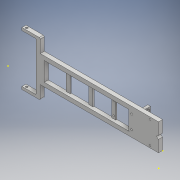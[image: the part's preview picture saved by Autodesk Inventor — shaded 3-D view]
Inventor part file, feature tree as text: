
AUTODESK INVENTOR PART (.ipt)
format: ipt  version: 2018 (Build 220112000, 112)  size: 670,208 bytes
history: native  units: mm
features: sketch x36, extrude x27, fillet x10, hole x6
ambient origin geometry x8: Origin, YZ Plane, XZ Plane, XY Plane, X Axis, Y Axis, Z Axis, Center Point
bodies: Solid1 (feature_tree)
feature tree (79):
  extrude  "Extrusion1"  Depth=50.0mm
  hole  "Hole1"  [1 undecoded]
  hole  "Hole2"  [1 undecoded]
  extrude  "Extrusion2"  Depth=25.0mm
  extrude  "Extrusion3"  Depth=25.0mm
  extrude  "Extrusion4"  Depth=5.0mm
  sketch  "Sketch7"  dims[d25=10.0mm d26=5.0mm]
  extrude  "Extrusion5"  Depth=5.0mm
  extrude  "Extrusion6"  Depth=35.0mm
  extrude  "Extrusion7"  Depth=35.0mm
  extrude  "Extrusion8"  Depth=35.0mm
  extrude  "Extrusion9"  Depth=2.0mm TaperAngle=0.0deg
  extrude  "Extrusion10"  Depth=7.5mm TaperAngle=0.0deg
  extrude  "Extrusion11"  Depth=10.0mm
  extrude  "Extrusion12"  Depth=7.5mm
  fillet  "Fillet1"  Radius=7.5mm
  fillet  "Fillet2"  Radius=25.0mm
  fillet  "Fillet3"  Radius=3.0mm
  fillet  "Fillet4"  Radius=3.2mm
  fillet  "Fillet5"  Radius=2.1mm
  fillet  "Fillet6"  Radius=5.5mm
  extrude  "Extrusion13"  Depth=92.5mm TaperAngle=0.0deg
  sketch  "Sketch17"  dims[d58=4.25mm d59=241.0mm d60=0.0mm]
  hole  "Hole3"  [1 undecoded]
  hole  "Hole4"  [1 undecoded]
  extrude  "Extrusion14"  Depth=5.0mm
  extrude  "Extrusion15"  Depth=91.25mm TaperAngle=0.0deg
  extrude  "Extrusion16"  Depth=30.0mm
  extrude  "Extrusion17"  Depth=2.5mm
  extrude  "Extrusion18"  Depth=14.55mm TaperAngle=0.0deg
  extrude  "Extrusion19"  Depth=0.1mm
  extrude  "Extrusion20"  Depth=3.25mm
  extrude  "Extrusion21"  Depth=3.25mm
  hole  "Hole5"  [1 undecoded]
  extrude  "Extrusion22"  Depth=2.0mm
  extrude  "Extrusion23"  Depth=15.0mm
  extrude  "Extrusion24"  Depth=10.0mm TaperAngle=0.0deg
  extrude  "Extrusion25"  Depth=2.0mm
  extrude  "Extrusion26"  Depth=100.0mm TaperAngle=0.0deg
  sketch  "Sketch34"  dims[d113=5.0mm d114=2.0mm d115=0.0mm]
  hole  "Hole6"  [1 undecoded]
  extrude  "Extrusion27"  Depth=5.5mm
  fillet  "Fillet7"  Radius=3.3mm
  fillet  "Fillet8"  Radius=3.3mm
  fillet  "Fillet9"  Radius=2.0mm
  fillet  "Fillet10"  Radius=5.5mm
  sketch  "Sketch1"  dims[d0=50.0mm d1=50.0mm]
  sketch  "Sketch2"  dims[d2=240.0mm d3=7.5mm]
  sketch  "Sketch3"  dims[d4=7.5mm d5=7.5mm d6=0.0mm]
  sketch  "Sketch4"  dims[d7=6.35mm d8=6.0mm d9=4.0mm d10=2.0mm d11=90.0deg d12=8.0mm d13=20.594885mm d14=25.0mm]
  sketch  "Sketch5"  dims[d15=3.3mm d16=6.0mm d17=4.0mm d18=2.0mm d19=90.0deg d20=8.0mm d21=20.594885mm d22=25.0mm]
  sketch  "Sketch6"  dims[d23=180.0deg d24=5.0mm]
  sketch  "Sketch8"  dims[d27=17.5mm d28=0.0mm d30=35.0mm]
  sketch  "Sketch9"  dims[d31=35.0mm d32=35.0mm]
  sketch  "Sketch10"  dims[d33=35.0mm d34=35.0mm]
  sketch  "Sketch11"  dims[d35=35.0mm d36=2.0mm d37=0.0mm]
  sketch  "Sketch12"  dims[d38=10.0mm d39=7.5mm d40=0.0mm]
  sketch  "Sketch13"  dims[d41=100.0mm d42=10.0mm]
  sketch  "Sketch14"  dims[d43=7.5mm d44=0.0mm d45=7.5mm d46=7.5mm d47=25.0mm d48=0.0mm d49=3.0mm d50=3.2mm d51=2.1mm d52=5.5mm]
  sketch  "Sketch15"  dims[d53=3.3mm d54=92.5mm d55=0.0mm]
  sketch  "Sketch16"  dims[d56=5.5mm d57=3.3mm]
  sketch  "Sketch18"  dims[d61=4.44mm d62=5.0mm]
  sketch  "Sketch19"  dims[d63=2.5mm d64=91.25mm d65=0.0mm]
  sketch  "Sketch20"  dims[d66=30.0mm d67=6.35mm]
  sketch  "Sketch21"  dims[d68=3.8mm d69=0.0mm d70=2.5mm]
  sketch  "Sketch22"  dims[d71=14.55mm d72=0.0mm d73=14.55mm d74=0.0mm]
  sketch  "Sketch23"  dims[d75=0.1mm d76=0.1mm]
  sketch  "Sketch24"  dims[d77=3.25mm d78=3.25mm]
  sketch  "Sketch25"  dims[d79=3.25mm d80=3.25mm]
  sketch  "Sketch26"  dims[d81=35.0mm d82=10.0mm]
  sketch  "Sketch27"  dims[d83=2.0mm d84=0.0mm d85=3.6mm]
  sketch  "Sketch28"  dims[d86=3.6mm]
  sketch  "Sketch29"  dims[d87=3.3mm d88=6.0mm d89=4.0mm d90=2.0mm d91=90.0deg d92=15.0mm d93=20.594885mm]
  sketch  "Sketch30"  dims[d94=3.3mm d95=6.0mm d96=4.0mm d97=2.0mm d98=90.0deg d99=15.0mm d100=20.594885mm d101=6.0mm]
  sketch  "Sketch31"  dims[d102=20.0mm d103=0.0mm d104=10.0mm d105=0.0mm]
  sketch  "Sketch32"  dims[d106=2.0mm d107=0.0mm d108=4.0mm]
  sketch  "Sketch33"  dims[d109=100.0mm d110=0.0mm d111=100.0mm d112=0.0mm]
  sketch  "Sketch35"  dims[d116=3.3mm d117=3.3mm d118=3.3mm d119=3.3mm d120=2.0mm d121=0.0mm d122=5.5mm d123=0.0mm]
  sketch  "Sketch36"  dims[d124=3.3mm d125=6.0mm d126=4.0mm d127=2.0mm d128=90.0deg d129=8.0mm d130=20.594885mm d131=42.0mm d132=17.0mm d133=21.0mm d135=8.5mm d136=15.825mm d137=3.5mm d138=21.0mm d139=3.3mm d140=3.3mm d141=3.3mm d142=10.0mm d143=0.0mm d144=7.5mm d145=0.0mm d146=100.0mm d147=0.0mm d148=42.0mm d149=7.5mm d150=7.5mm d151=0.0mm d152=34.0mm d153=7.5mm d154=75.0mm d155=25.0mm d156=5.0mm d157=5.0mm d158=7.5mm d159=0.0mm d160=4.0mm d161=2.0mm d162=4.0mm d163=4.0mm d164=6.0mm d165=4.0mm d166=2.0mm d167=90.0deg d168=800.0mm d169=20.594885mm d170=700.0mm d171=0.0mm d172=2.0mm d173=2.0mm d174=2.0mm d175=2.0mm]
note: 6 required parameter values undecoded (feature->parameter linkage not recoverable at this tier; creation-order binding heuristic only, values carry confidence <= 0.55)
